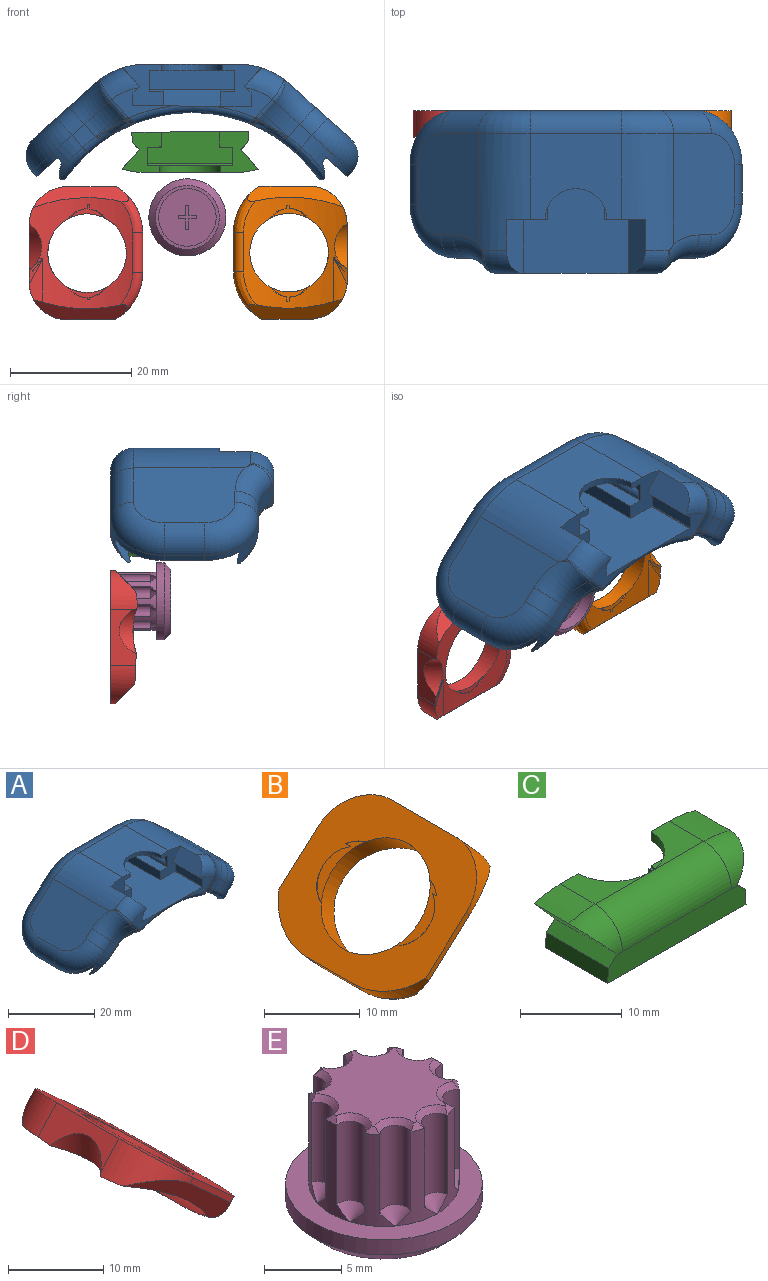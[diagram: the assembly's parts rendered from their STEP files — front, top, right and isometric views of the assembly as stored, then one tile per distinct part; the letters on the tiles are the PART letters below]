
ASSEMBLY  parts=5 mates=4
PART A: 164 faces, bbox 57.7x34x23.8 mm
  f0: cylinder r=10.41mm len=20.83mm, axis (0.67,0,-0.74), area 140.7mm2, adj f70,f71,f73,f74,f116,f122,f149,f150
  f1: plane 15.75x3.43mm, normal (1,0,0), area 24.3mm2, adj f5,f111,f112,f123,f124,f148,f150,f162
  f2: plane 15.75x3.43mm, normal (-1,0,0), area 24.3mm2, adj f3,f111,f115,f123,f124,f153,f155,f163
  f3: plane 6.94x6.69mm, normal (0,-1,0), area 27mm2, adj f2,f4,f6,f106,f107,f108,f109,f110
  f4: plane 15.11x14.14mm, normal (0,0,1), area 173.1mm2, adj f3,f5,f6,f7,f91,f125
  f5: plane 6.88x6.69mm, normal (0,-1,0), area 26.8mm2, adj f1,f4,f7,f103,f104,f105,f106,f111
  f6: cylinder r=12.7mm len=19.22mm, axis (0,1,0), area 158.4mm2, adj f3,f4,f43,f93,f100,f110,f137
  f7: cylinder r=12.7mm len=19.22mm, axis (0,1,0), area 158.4mm2, adj f4,f5,f11,f42,f89,f103,f126
  f8: plane 9.84x4.88mm, normal (0,-1,0), area 14.3mm2, adj f10,f11,f104,f105,f106,f129,f130,f131
  f9: plane 9.64x4.88mm, normal (0,-1,0), area 14mm2, adj f10,f100,f106,f107,f108,f109,f140,f141
  f10: torus R=26.58mm, axis (0,-1,0), area 38.5mm2, adj f8,f9,f12,f106,f134,f135,f136,f145
  f11: torus R=8.89mm, axis (0,-1,0), area 27.7mm2, adj f7,f8,f103,f104,f127,f128
  f12: cylinder r=25.31mm len=40.92mm, axis (0,1,0), area 321.2mm2, adj f10,f14,f20,f25,f37,f39,f60,f61
  f13: cylinder r=13.97mm len=5.07mm, axis (0,1,0), area 14.8mm2, adj f16,f26,f31,f46,f53,f74
  f14: torus R=39.28mm, axis (0,1,0), area 76.6mm2, adj f12,f16,f17,f44,f64,f65
  f15: cylinder r=13.97mm len=5.07mm, axis (0,1,0), area 14.8mm2, adj f17,f21,f30,f48,f58,f76
  f16: bspline ~6.48x5.29mm, area 7.5mm2, adj f13,f14,f46,f65,f74
  f17: bspline ~8.33x6.71mm, area 7.5mm2, adj f14,f15,f48,f64,f76
  f18: plane 22.35x6.9mm, normal (-0.67,0,-0.74), area 34.8mm2, adj f19,f22,f28,f33,f35,f117
  f19: plane 6.96x6.56mm, normal (0,1,0), area 8.6mm2, adj f18,f20,f35,f75,f117
  f20: plane 15.09x12.05mm, normal (0.47,0.71,0.53), area 38.8mm2, adj f12,f19,f35,f39,f75
  f21: plane 14.06x11.28mm, normal (0.47,-0.71,0.53), area 37.8mm2, adj f15,f22,f30,f33,f38,f76
  f22: plane 6.71x6.34mm, normal (0,-1,0), area 8.3mm2, adj f18,f21,f33,f76,f117
  f23: plane 22.35x6.9mm, normal (0.67,0,-0.74), area 34.8mm2, adj f24,f27,f29,f32,f34,f116
  f24: plane 6.96x6.56mm, normal (0,1,0), area 8.6mm2, adj f23,f25,f34,f73,f116
  f25: plane 15.09x12.05mm, normal (-0.47,0.71,0.53), area 38.8mm2, adj f12,f24,f34,f37,f73
  f26: plane 14.06x11.28mm, normal (-0.47,-0.71,0.53), area 37.8mm2, adj f13,f27,f31,f32,f36,f74
  f27: plane 6.71x6.34mm, normal (0,-1,0), area 8.3mm2, adj f23,f26,f32,f74,f116
  f28: plane 6.52x0.85mm, normal (0.74,0,-0.67), area 7.5mm2, adj f18,f33,f35,f98
  f29: plane 6.52x0.85mm, normal (-0.74,0,-0.67), area 7.5mm2, adj f23,f32,f34,f90
  f30: cylinder r=25.31mm len=9.51mm, axis (0,1,0), area 22.3mm2, adj f15,f21,f38,f59
  f31: cylinder r=25.31mm len=9.51mm, axis (0,1,0), area 22.3mm2, adj f13,f26,f36,f55
  f32: cylinder r=8.89mm len=8.89mm, axis (0.67,0,-0.74), area 23.3mm2, adj f23,f26,f27,f29,f36,f50,f88
  f33: cylinder r=8.89mm len=8.89mm, axis (0.67,0,0.74), area 23.3mm2, adj f18,f21,f22,f28,f38,f50,f97
  f34: cylinder r=8.89mm len=8.89mm, axis (0.67,0,-0.74), area 24.1mm2, adj f23,f24,f25,f29,f37,f41,f92
  f35: cylinder r=8.89mm len=8.89mm, axis (0.67,0,0.74), area 24.1mm2, adj f18,f19,f20,f28,f39,f40,f99
  f36: bspline ~7.85x7.18mm, area 13.1mm2, adj f26,f31,f32,f55
  f37: bspline ~8.21x7.4mm, area 13.8mm2, adj f12,f25,f34,f60
  f38: bspline ~7.41x6.89mm, area 13.1mm2, adj f21,f30,f33,f59
  f39: bspline ~7.85x7.18mm, area 13.8mm2, adj f12,f20,f35,f63
  f40: plane 3.86x3.78mm, normal (0,-1,0), area 7.3mm2, adj f35,f63,f77,f101
  f41: plane 3.86x3.78mm, normal (0,-1,0), area 7.3mm2, adj f34,f60,f82,f94
  f42: plane 18.19x10.02mm, normal (-0.67,0,0.74), area 216.5mm2, adj f7,f87,f88,f90,f92,f94,f96
  f43: plane 18.19x10.02mm, normal (0.67,0,0.74), area 216.5mm2, adj f6,f95,f97,f98,f99,f101,f102
  f44: cone r=29.12mm half-angle=20.6deg, axis (0,1,0), area 46.9mm2, adj f14,f45,f46,f48
  f45: torus R=15.15mm, axis (0,-1,0), area 0.3mm2, adj f44,f47,f49,f54
  f46: bspline ~10.91x6.7mm, area 18.8mm2, adj f13,f16,f44,f47,f51
  f47: bspline ~5.27x4.34mm, area 0mm2, adj f45,f46,f52
  f48: bspline ~9.02x6.04mm, area 18.8mm2, adj f15,f17,f44,f49,f57
  f49: bspline ~4.48x4.13mm, area 0mm2, adj f45,f48,f56
  f50: plane 39.49x9.87mm, normal (0,1,0), area 99.5mm2, adj f32,f33,f51,f52,f53,f54,f55,f56
  f51: bspline ~6.72x4.14mm, area 8.6mm2, adj f46,f50,f52,f53
  f52: bspline ~1.28x0.87mm, area 0.3mm2, adj f47,f50,f51,f54
  f53: torus R=12.7mm, axis (0,-1,0), area 10.1mm2, adj f13,f50,f51,f55
  f54: torus R=29.45mm, axis (0,-1,0), area 7.9mm2, adj f45,f50,f52,f56
  f55: torus R=26.58mm, axis (0,-1,0), area 15.5mm2, adj f31,f36,f50,f53
  f56: bspline ~1.25x0.84mm, area 0.3mm2, adj f49,f50,f54,f57
  f57: bspline ~6.78x4.19mm, area 8.6mm2, adj f48,f50,f56,f58
  f58: torus R=12.7mm, axis (0,-1,0), area 10.1mm2, adj f15,f50,f57,f59
  f59: torus R=26.58mm, axis (0,-1,0), area 15.5mm2, adj f30,f38,f50,f58
  f60: torus R=26.58mm, axis (0,1,0), area 8.8mm2, adj f12,f37,f41,f83,f84,f85,f86
  f61: cylinder r=1.27mm len=2.6mm, axis (0,1,0), area 0.4mm2, adj f12,f85,f135
  f62: cylinder r=1.27mm len=2.6mm, axis (0,1,0), area 0.4mm2, adj f12,f80,f147
  f63: torus R=26.58mm, axis (0,1,0), area 8.8mm2, adj f12,f39,f40,f78,f79,f80,f81
  f64: plane 9.88x2.32mm, normal (0.74,0,-0.67), area 26.5mm2, adj f12,f14,f17,f75,f76,f119
  f65: plane 9.88x2.46mm, normal (-0.74,0,-0.67), area 28.4mm2, adj f12,f14,f16,f71,f73,f74
  f66: plane 19.9x14.81mm, normal (-0.67,0,-0.74), area 308.2mm2, adj f121,f160,f161
  f67: plane 9.97x0.94mm, normal (0.67,0,0.74), area 8.5mm2, adj f68,f72
  f68: cylinder r=10.41mm len=20.83mm, axis (-0.67,0,-0.74), area 140.9mm2, adj f67,f72,f75,f76,f117,f118,f120,f121
  f69: plane 19.9x14.81mm, normal (0.67,0,-0.74), area 308.2mm2, adj f122,f158,f159
  f70: plane 9.97x0.94mm, normal (-0.67,0,0.74), area 8.5mm2, adj f0,f71
  f71: plane 16.96x4.4mm, normal (-1,0,0.05), area 33.5mm2, adj f0,f65,f70,f73,f74
  f72: plane 15.86x3.38mm, normal (1,0,0.05), area 30.3mm2, adj f67,f68,f118,f119,f120
  f73: cylinder r=6.35mm len=8.43mm, axis (0.67,0,-0.74), area 24.1mm2, adj f0,f12,f24,f25,f65,f71,f116
  f74: cylinder r=6.35mm len=8.17mm, axis (-0.67,0,0.74), area 23.2mm2, adj f0,f13,f16,f26,f27,f65,f71,f116
  f75: cylinder r=6.35mm len=8.43mm, axis (-0.67,0,-0.74), area 23.3mm2, adj f12,f19,f20,f64,f68,f117,f118
  f76: cylinder r=6.35mm len=8.17mm, axis (0.67,0,0.74), area 22.3mm2, adj f15,f17,f21,f22,f64,f68,f117,f120
  f77: cylinder r=7.62mm len=5.86mm, axis (-0.67,0,-0.74), area 16.5mm2, adj f40,f78,f102,f139,f140
  f78: bspline ~5.88x4.79mm, area 3.6mm2, adj f63,f77,f79,f141
  f79: bspline ~5.37x3.39mm, area 1.5mm2, adj f63,f78,f81,f142
  f80: bspline ~4.93x4.83mm, area 4.7mm2, adj f62,f63,f81,f146
  f81: bspline ~6.23x3.41mm, area 7.9mm2, adj f63,f79,f80,f143,f144,f145
  f82: cylinder r=7.62mm len=5.86mm, axis (0.67,0,-0.74), area 16.5mm2, adj f41,f83,f96,f128,f129
  f83: bspline ~5.39x4.52mm, area 3.6mm2, adj f60,f82,f84,f130
  f84: bspline ~5.35x3.43mm, area 1.5mm2, adj f60,f83,f86,f131
  f85: bspline ~4.93x4.83mm, area 4.7mm2, adj f60,f61,f86,f136
  f86: bspline ~6.25x3.43mm, area 7.9mm2, adj f60,f84,f85,f132,f133,f134
  f87: cylinder r=3.81mm len=8.79mm, axis (-0.74,0,-0.67), area 50.3mm2, adj f42,f50,f88,f89
  f88: torus R=5.08mm, axis (0.67,0,-0.74), area 70.6mm2, adj f32,f42,f87,f90
  f89: torus R=8.89mm, axis (0,-1,0), area 49.6mm2, adj f7,f50,f87,f91
  f90: cylinder r=3.81mm len=6.52mm, axis (0,1,0), area 39mm2, adj f29,f42,f88,f92
  f91: cylinder r=3.81mm len=15.11mm, axis (1,0,0), area 90.4mm2, adj f4,f50,f89,f93
  f92: torus R=5.08mm, axis (0.67,0,-0.74), area 70.6mm2, adj f34,f42,f90,f94
  f93: torus R=8.89mm, axis (0,-1,0), area 49.6mm2, adj f6,f50,f91,f95
  f94: cylinder r=3.81mm len=4.65mm, axis (-0.74,0,-0.67), area 16.3mm2, adj f41,f42,f92,f96
  f95: cylinder r=3.81mm len=8.79mm, axis (-0.74,0,0.67), area 50.3mm2, adj f43,f50,f93,f97
  f96: torus R=11.43mm, axis (0.67,0,-0.74), area 37.2mm2, adj f42,f82,f94,f126,f127
  f97: torus R=5.08mm, axis (-0.67,0,-0.74), area 70.6mm2, adj f33,f43,f95,f98
  f98: cylinder r=3.81mm len=6.52mm, axis (0,-1,0), area 39mm2, adj f28,f43,f97,f99
  f99: torus R=5.08mm, axis (-0.67,0,-0.74), area 70.6mm2, adj f35,f43,f98,f101
  f100: torus R=8.89mm, axis (0,-1,0), area 27.7mm2, adj f6,f9,f109,f110,f138,f139
  f101: cylinder r=3.81mm len=4.65mm, axis (-0.74,0,0.67), area 16.3mm2, adj f40,f43,f99,f102
  f102: torus R=11.43mm, axis (-0.67,0,-0.74), area 37.2mm2, adj f43,f77,f101,f137,f138
  f103: plane 8.89x3.14mm, normal (0.74,0,0.67), area 34.1mm2, adj f5,f7,f11,f104
  f104: plane 8.89x1.11mm, normal (0.67,0,-0.74), area 13.3mm2, adj f5,f8,f11,f103,f105
  f105: plane 8.89x2.11mm, normal (1,0,-0.05), area 18.8mm2, adj f5,f8,f104,f106
  f106: plane 20.03x19.46mm, normal (0,0,1), area 278.7mm2, adj f3,f5,f8,f9,f10,f105,f107,f113
  f107: plane 8.89x0.23mm, normal (0,0,1), area 2mm2, adj f3,f9,f106,f108
  f108: plane 8.89x2.19mm, normal (-1,0,-0.05), area 19.5mm2, adj f3,f9,f107,f109
  f109: plane 8.89x1.11mm, normal (-0.67,0,-0.74), area 13.3mm2, adj f3,f9,f100,f108,f110
  f110: plane 8.89x3.14mm, normal (-0.74,0,0.67), area 34.1mm2, adj f3,f6,f100,f109
  f111: plane 15.75x14.1mm, normal (0,0,-1), area 181.5mm2, adj f1,f2,f3,f5,f123,f125
  f112: plane 15.11x2.29mm, normal (0,0,1), area 34.6mm2, adj f1,f5,f113,f124
  f113: plane 15.11x2.39mm, normal (1,0,0), area 31.3mm2, adj f5,f106,f112,f124
  f114: plane 15.11x2.42mm, normal (-1,0,0), area 31.7mm2, adj f3,f106,f115,f124
  f115: plane 15.11x2.29mm, normal (0,0,1), area 34.6mm2, adj f2,f3,f114,f124
  f116: cone r=11.43mm half-angle=53.1deg, axis (0.67,0,-0.74), area 51.3mm2, adj f0,f23,f24,f27,f73,f74
  f117: cone r=11.43mm half-angle=53.1deg, axis (-0.67,0,-0.74), area 51.3mm2, adj f18,f19,f22,f68,f75,f76
  f118: bspline ~3.66x1.79mm, area 1.4mm2, adj f68,f72,f75,f119
  f119: cylinder r=0.46mm len=9.65mm, axis (0,1,0), area 3.5mm2, adj f64,f72,f118,f120
  f120: bspline ~3.66x1.79mm, area 1.4mm2, adj f68,f72,f76,f119
  f121: cone r=10.41mm half-angle=45deg, axis (-0.67,0,-0.74), area 45.9mm2, adj f66,f68,f153
  f122: cone r=10.41mm half-angle=45deg, axis (0.67,0,-0.74), area 45.9mm2, adj f0,f69,f148
  f123: plane 14.1x3.05mm, normal (0,-1,0), area 43mm2, adj f1,f2,f111,f124
  f124: plane 14.1x4.67mm, normal (0,-0.51,0.86), area 55mm2, adj f1,f2,f106,f112,f113,f114,f115,f123
  f125: cylinder r=5.08mm len=10.16mm, axis (0,0,1), area 17mm2, adj f3,f4,f5,f111
  f126: bspline ~1.74x1.04mm, area 0.1mm2, adj f7,f96,f127
  f127: bspline ~4.04x3.97mm, area 3.3mm2, adj f11,f96,f126,f128
  f128: bspline ~1.32x1.28mm, area 0mm2, adj f11,f82,f127,f129
  f129: cylinder r=1.02mm len=2.52mm, axis (0.67,0,-0.74), area 2.2mm2, adj f8,f82,f128,f130
  f130: bspline ~1.65x1.59mm, area 0.9mm2, adj f8,f83,f129,f131
  f131: bspline ~0.94x0.85mm, area 0.2mm2, adj f8,f84,f130,f132
  f132: bspline ~0.87x0.53mm, area 0.1mm2, adj f86,f131,f133
  f133: bspline ~0.99x0.71mm, area 0.3mm2, adj f8,f86,f132,f134
  f134: bspline ~1.25x1.17mm, area 0.9mm2, adj f10,f86,f133,f136
  f135: bspline ~0.61x0.6mm, area 0mm2, adj f10,f61,f136
  f136: bspline ~0.85x0.51mm, area 0.2mm2, adj f10,f85,f134,f135
  f137: bspline ~3.54x1.99mm, area 0.1mm2, adj f6,f102,f138
  f138: bspline ~4.04x3.97mm, area 3.3mm2, adj f100,f102,f137,f139
  f139: bspline ~1.32x1.28mm, area 0mm2, adj f77,f100,f138,f140
  f140: cylinder r=1.02mm len=2.52mm, axis (-0.67,0,-0.74), area 2.2mm2, adj f9,f77,f139,f141
  f141: bspline ~2.3x2.18mm, area 0.9mm2, adj f9,f78,f140,f142
  f142: bspline ~0.94x0.85mm, area 0.2mm2, adj f9,f79,f141,f143
  f143: bspline ~0.87x0.53mm, area 0.1mm2, adj f81,f142,f144
  f144: bspline ~1x0.74mm, area 0.2mm2, adj f9,f81,f143,f145
  f145: bspline ~1.25x1.19mm, area 0.9mm2, adj f10,f81,f144,f146
  f146: bspline ~0.91x0.55mm, area 0.2mm2, adj f10,f80,f145,f147
  f147: bspline ~0.61x0.6mm, area 0mm2, adj f10,f62,f146
  f148: extruded ~13.72x4.79mm, area 54.2mm2, adj f1,f122,f149,f150,f151,f152,f162
  f149: plane 11.88x3.52mm, normal (0,0,1), area 25.3mm2, adj f0,f148,f150,f152,f162
  f150: plane 4.79x1.79mm, normal (0,1,0), area 2.8mm2, adj f0,f1,f148,f149,f151,f162
  f151: plane 0.77x0.64mm, normal (1,0,0), area 0.1mm2, adj f0,f148,f150
  f152: plane 1.9x0.83mm, normal (1,0,0), area 0.4mm2, adj f0,f148,f149
  f153: extruded ~13.72x4.79mm, area 54.2mm2, adj f2,f121,f154,f155,f156,f157,f163
  f154: plane 11.89x3.53mm, normal (0,0,1), area 25.3mm2, adj f68,f153,f155,f157,f163
  f155: plane 4.79x1.79mm, normal (0,1,0), area 2.8mm2, adj f2,f68,f153,f154,f156,f163
  f156: plane 0.77x0.64mm, normal (-1,0,0), area 0.1mm2, adj f68,f153,f155
  f157: plane 1.9x0.83mm, normal (-1,0,0), area 0.4mm2, adj f68,f153,f154
  f158: plane 2.25x0.04mm, normal (1,0,0), area 0.1mm2, adj f69,f159
  f159: extruded ~2.25x0.04mm, area 0mm2, adj f69,f158
  f160: plane 2.25x0.04mm, normal (-1,0,0), area 0.1mm2, adj f66,f161
  f161: extruded ~2.25x0.04mm, area 0mm2, adj f66,f160
  f162: cylinder r=1.27mm len=13.72mm, axis (0,-1,0), area 25.5mm2, adj f1,f148,f149,f150
  f163: cylinder r=1.27mm len=13.72mm, axis (0,1,0), area 25.5mm2, adj f2,f153,f154,f155
PART B: 36 faces, bbox 20x23.9x18.1 mm
  f0: cylinder r=25.31mm len=18.28mm, axis (0,1,0), area 126.4mm2, adj f2,f3,f4,f5,f6,f7,f8,f9
  f1: plane 21.95x13.89mm, normal (-0.67,0,0.74), area 225.5mm2, adj f10,f11,f13,f14,f17,f18,f19,f22
  f2: cylinder r=3.24mm len=1.7mm, axis (0.67,0,-0.74), area 0mm2, adj f0,f9,f34
  f3: cylinder r=3.24mm len=2.01mm, axis (0.67,0,-0.74), area 0.1mm2, adj f0,f8,f29,f34
  f4: cylinder r=3.24mm len=2.01mm, axis (0.67,0,-0.74), area 0.1mm2, adj f0,f6,f29,f32
  f5: cylinder r=3.24mm len=1.7mm, axis (0.67,0,-0.74), area 0mm2, adj f0,f7,f32
  f6: bspline ~4.55x2.83mm, area 0.3mm2, adj f0,f4,f29
  f7: bspline ~4.55x2.65mm, area 0.3mm2, adj f0,f5,f29
  f8: bspline ~4.55x2.83mm, area 0.3mm2, adj f0,f3,f29
  f9: bspline ~4.55x2.65mm, area 0.3mm2, adj f0,f2,f29
  f10: cone r=3.75mm half-angle=45deg, axis (-0.67,0,0.74), area 0.3mm2, adj f1,f29,f35
  f11: cone r=3.75mm half-angle=45deg, axis (-0.67,0,0.74), area 0.3mm2, adj f1,f29,f31
  f12: torus R=39.28mm, axis (0,1,0), area 0.4mm2, adj f0,f13,f25,f28
  f13: plane 9.51x3.46mm, normal (0.74,0,0.67), area 24.4mm2, adj f1,f12,f14,f25,f27,f28
  f14: cylinder r=6.35mm len=7.69mm, axis (-0.67,0,0.74), area 26.3mm2, adj f0,f1,f13,f23,f24,f28
  f15: cylinder r=1.27mm len=6.52mm, axis (0,1,0), area 15.5mm2, adj f0,f16,f18,f20
  f16: bspline ~9.5x4.45mm, area 15.4mm2, adj f0,f15,f17,f24
  f17: cylinder r=8.89mm len=7.63mm, axis (0.67,0,-0.74), area 18.3mm2, adj f1,f16,f18,f23,f24
  f18: plane 6.52x1.85mm, normal (-0.74,0,-0.67), area 16.2mm2, adj f1,f15,f17,f19
  f19: cylinder r=8.89mm len=7.8mm, axis (0.67,0,-0.74), area 18.8mm2, adj f1,f18,f20,f21,f22
  f20: bspline ~9.84x4.9mm, area 16.1mm2, adj f0,f15,f19,f21
  f21: plane 14.42x11.77mm, normal (0.47,0.71,-0.53), area 39.2mm2, adj f0,f19,f20,f22,f26,f27
  f22: plane 6.23x5.71mm, normal (0,1,0), area 5.6mm2, adj f1,f19,f21,f27
  f23: plane 6.45x5.91mm, normal (0,-1,0), area 5.8mm2, adj f1,f14,f17,f24
  f24: plane 14.65x11.84mm, normal (0.47,-0.71,-0.53), area 40mm2, adj f0,f14,f16,f17,f23
  f25: bspline ~4.3x3.46mm, area 3mm2, adj f12,f13,f26,f27
  f26: cylinder r=13.97mm len=7.21mm, axis (0,1,0), area 10.1mm2, adj f0,f21,f25,f27
  f27: cylinder r=6.35mm len=7.48mm, axis (0.67,0,-0.74), area 25.7mm2, adj f1,f13,f21,f22,f25,f26
  f28: cylinder r=4.57mm len=7.54mm, axis (0,0,-1), area 17.8mm2, adj f0,f12,f13,f14
  f29: cylinder r=6.48mm len=12.95mm, axis (0.68,0,-0.74), area 120.6mm2, adj f0,f1,f3,f4,f6,f7,f8,f9
  f30: cylinder r=4.51mm len=2.07mm, axis (0.68,0,-0.74), area 0mm2, adj f1,f29,f31
  f31: plane 5.8x5.31mm, normal (-0.68,0,0.74), area 7.7mm2, adj f1,f11,f29,f30
  f32: plane 3.94x3.61mm, normal (0.68,0,-0.74), area 3.5mm2, adj f0,f4,f5,f29
  f33: cylinder r=4.41mm len=1.85mm, axis (0.68,0,-0.74), area 0mm2, adj f1,f29,f35
  f34: plane 3.94x3.61mm, normal (0.68,0,-0.74), area 3.4mm2, adj f0,f2,f3,f29
  f35: plane 5.75x5.26mm, normal (-0.68,0,0.74), area 7.5mm2, adj f1,f10,f29,f33
PART C: 31 faces, bbox 22.5x8.6x6.9 mm
  f0: plane 6.71x6.45mm, normal (0,1,0), area 24.9mm2, adj f2,f3,f9,f10,f14,f16,f17,f18
  f1: plane 7.55x4.83mm, normal (0,0,1), area 17.5mm2, adj f4,f5,f13,f26
  f2: plane 7.55x4.83mm, normal (0,0,1), area 17.5mm2, adj f0,f5,f14,f26
  f3: plane 19.21x8.64mm, normal (0,0,-1), area 105.4mm2, adj f0,f4,f7,f15,f16,f19,f20,f24
  f4: plane 6.65x6.45mm, normal (0,1,0), area 24.7mm2, adj f1,f3,f11,f12,f13,f15,f20,f21
  f5: cylinder r=3.81mm len=15.11mm, axis (1,0,0), area 90.4mm2, adj f1,f2,f6,f7,f8
  f6: torus R=8.89mm, axis (0,-1,0), area 15.8mm2, adj f5,f7,f9,f10,f14
  f7: plane 19.21x2.9mm, normal (0,-1,0), area 53.4mm2, adj f3,f5,f6,f8,f9,f12,f15,f16
  f8: torus R=8.89mm, axis (0,-1,0), area 15.8mm2, adj f5,f7,f11,f12,f13
  f9: plane 8.64x1.21mm, normal (0.67,0,0.74), area 14.1mm2, adj f0,f6,f7,f10,f16
  f10: plane 8.64x3.23mm, normal (0.74,0,-0.67), area 34mm2, adj f0,f6,f9,f14
  f11: plane 8.64x3.23mm, normal (-0.74,0,-0.67), area 34mm2, adj f4,f8,f12,f13
  f12: plane 8.64x1.21mm, normal (-0.67,0,0.74), area 14.1mm2, adj f4,f7,f8,f11,f15
  f13: cylinder r=12.7mm len=4.83mm, axis (0,1,0), area 17.9mm2, adj f1,f4,f8,f11
  f14: cylinder r=12.7mm len=4.83mm, axis (0,1,0), area 17.9mm2, adj f0,f2,f6,f10
  f15: plane 8.64x1.78mm, normal (-1,0,0.05), area 15.4mm2, adj f3,f4,f7,f12
  f16: plane 8.64x1.85mm, normal (1,0,0.05), area 16mm2, adj f0,f3,f7,f9
  f17: plane 6.35x3.05mm, normal (-1,0,0), area 19.3mm2, adj f0,f18,f23,f24,f25
  f18: plane 6.35x2.29mm, normal (0,0,1), area 14.2mm2, adj f0,f17,f19,f24,f30
  f19: plane 6.35x2.57mm, normal (-1,0,0), area 16mm2, adj f0,f3,f18,f24,f29,f30
  f20: plane 6.35x2.54mm, normal (1,0,0), area 15.8mm2, adj f3,f4,f21,f24,f27,f28
  f21: plane 6.35x2.29mm, normal (0,0,1), area 14.2mm2, adj f4,f20,f22,f24,f27
  f22: plane 6.35x3.05mm, normal (1,0,0), area 19.3mm2, adj f4,f21,f23,f24,f25
  f23: plane 14.1x5.97mm, normal (0,0,-1), area 46.2mm2, adj f0,f4,f17,f22,f25,f26
  f24: plane 14.1x5.24mm, normal (0,1,0), area 62mm2, adj f3,f17,f18,f19,f20,f21,f22,f25
  f25: plane 14.1x0.38mm, normal (0,0.71,-0.71), area 7.6mm2, adj f17,f22,f23,f24
  f26: cylinder r=5.08mm len=10.15mm, axis (0,0,1), area 16.5mm2, adj f0,f1,f2,f4,f23
  f27: cylinder r=5.08mm len=1.51mm, axis (0,0,1), area 0.4mm2, adj f4,f20,f21,f28
  f28: plane 1.51x0.31mm, normal (0,0,1), area 0.3mm2, adj f4,f20,f27
  f29: plane 1.51x0.31mm, normal (0,0,1), area 0.3mm2, adj f0,f19,f30
  f30: cylinder r=5.08mm len=1.51mm, axis (0,0,1), area 0.4mm2, adj f0,f18,f19,f29
PART D: 37 faces, bbox 20x23.9x18.1 mm
  f0: cylinder r=3.24mm len=1.7mm, axis (-0.67,0,-0.74), area 0mm2, adj f5,f7,f36
  f1: cone r=3.75mm half-angle=45deg, axis (0.67,0,0.74), area 0.3mm2, adj f22,f29,f35
  f2: cylinder r=3.24mm len=2.01mm, axis (-0.67,0,-0.74), area 0.1mm2, adj f5,f10,f29,f33
  f3: cone r=3.75mm half-angle=45deg, axis (0.67,0,0.74), area 0.8mm2, adj f22,f29,f30,f32
  f4: torus R=39.28mm, axis (0,1,0), area 0.4mm2, adj f5,f19,f26,f28
  f5: cylinder r=25.31mm len=18.28mm, axis (0,1,0), area 126.6mm2, adj f0,f2,f4,f6,f7,f8,f9,f10
  f6: cylinder r=6.35mm len=7.69mm, axis (-0.67,0,-0.74), area 26.3mm2, adj f5,f22,f23,f24,f26,f28
  f7: bspline ~4.55x2.65mm, area 0.3mm2, adj f0,f5,f29
  f8: bspline ~4.55x2.83mm, area 0.3mm2, adj f5,f15,f29
  f9: bspline ~4.55x2.65mm, area 0.3mm2, adj f5,f16,f29
  f10: bspline ~4.55x2.83mm, area 0.3mm2, adj f2,f5,f29
  f11: cylinder r=1.27mm len=6.52mm, axis (0,1,0), area 15.5mm2, adj f5,f12,f13,f17
  f12: bspline ~9.03x3.93mm, area 15.4mm2, adj f5,f11,f14,f24
  f13: plane 6.52x1.85mm, normal (0.74,0,-0.67), area 16.2mm2, adj f11,f14,f18,f22
  f14: cylinder r=8.89mm len=7.63mm, axis (0.67,0,0.74), area 18.3mm2, adj f12,f13,f22,f23,f24
  f15: cylinder r=3.24mm len=2.01mm, axis (-0.67,0,-0.74), area 0.1mm2, adj f5,f8,f29,f36
  f16: cylinder r=3.24mm len=1.7mm, axis (-0.67,0,-0.74), area 0mm2, adj f5,f9,f33
  f17: bspline ~9.5x4.45mm, area 16.1mm2, adj f5,f11,f18,f20
  f18: cylinder r=8.89mm len=7.8mm, axis (0.67,0,0.74), area 18.8mm2, adj f13,f17,f20,f21,f22
  f19: bspline ~4.3x3.46mm, area 3mm2, adj f4,f25,f26,f27
  f20: plane 14.42x11.78mm, normal (-0.47,0.71,-0.53), area 39.1mm2, adj f5,f17,f18,f21,f25,f27
  f21: plane 6.23x5.71mm, normal (0,1,0), area 5.6mm2, adj f18,f20,f22,f27
  f22: plane 21.95x13.9mm, normal (0.67,0,0.74), area 225.9mm2, adj f1,f3,f6,f13,f14,f18,f21,f23
  f23: plane 6.45x5.91mm, normal (0,-1,0), area 5.8mm2, adj f6,f14,f22,f24
  f24: plane 14.65x11.84mm, normal (-0.47,-0.71,-0.53), area 40mm2, adj f5,f6,f12,f14,f23
  f25: cylinder r=13.97mm len=7.21mm, axis (0,1,0), area 10.1mm2, adj f5,f19,f20,f27
  f26: plane 9.51x3.46mm, normal (-0.74,0,0.67), area 24.4mm2, adj f4,f6,f19,f22,f27,f28
  f27: cylinder r=6.35mm len=7.48mm, axis (0.67,0,0.74), area 25.7mm2, adj f19,f20,f21,f22,f25,f26
  f28: cylinder r=4.57mm len=7.54mm, axis (0,0,-1), area 17.8mm2, adj f4,f5,f6,f26
  f29: cylinder r=6.48mm len=12.95mm, axis (-0.68,0,-0.74), area 120.4mm2, adj f1,f2,f3,f5,f7,f8,f9,f10
  f30: plane 5.37x4.91mm, normal (0.68,0,0.74), area 6.7mm2, adj f3,f22,f29,f31,f32
  f31: cylinder r=4.07mm len=1.12mm, axis (-0.68,0,-0.74), area 0mm2, adj f22,f29,f30
  f32: cylinder r=4.07mm len=3.48mm, axis (-0.68,0,-0.74), area 0mm2, adj f3,f30
  f33: plane 3.94x3.61mm, normal (-0.68,0,-0.74), area 3.3mm2, adj f2,f5,f16,f29
  f34: cylinder r=4.48mm len=2.21mm, axis (-0.68,0,-0.74), area 0mm2, adj f22,f29,f35
  f35: plane 5.85x5.36mm, normal (0.68,0,0.74), area 7.8mm2, adj f1,f22,f29,f34
  f36: plane 3.94x3.61mm, normal (-0.68,0,-0.74), area 3.5mm2, adj f0,f5,f15,f29
PART E: 70 faces, bbox 12.7x12.7x9.9 mm
  f0: plane 9.47x9.47mm, normal (0,0,-1), area 67.3mm2, adj f24,f36,f37,f38,f39,f40,f41,f42
  f1: cylinder r=1.02mm len=6.27mm, axis (0,0,-1), area 18.7mm2, adj f2,f20,f33,f68
  f2: cylinder r=4.85mm len=7.24mm, axis (0,0,-1), area 8.3mm2, adj f1,f3,f22,f32,f33,f66
  f3: cylinder r=1.02mm len=6.27mm, axis (0,0,-1), area 18.7mm2, adj f2,f4,f32,f64
  f4: cylinder r=4.85mm len=7.24mm, axis (0,0,-1), area 8.3mm2, adj f3,f5,f22,f31,f32,f62
  f5: cylinder r=1.02mm len=6.27mm, axis (0,0,-1), area 18.7mm2, adj f4,f6,f31,f60
  f6: cylinder r=4.85mm len=7.24mm, axis (0,0,-1), area 8.3mm2, adj f5,f7,f22,f30,f31,f58
  f7: cylinder r=1.02mm len=6.27mm, axis (0,0,-1), area 18.7mm2, adj f6,f8,f30,f56
  f8: cylinder r=4.85mm len=7.24mm, axis (0,0,-1), area 8.3mm2, adj f7,f9,f22,f29,f30,f54
  f9: cylinder r=1.02mm len=6.27mm, axis (0,0,-1), area 18.7mm2, adj f8,f10,f29,f52
  f10: cylinder r=4.85mm len=7.24mm, axis (0,0,-1), area 8.3mm2, adj f9,f11,f22,f28,f29,f50
  f11: cylinder r=1.02mm len=6.27mm, axis (0,0,-1), area 18.7mm2, adj f10,f12,f28,f49
  f12: cylinder r=4.85mm len=7.24mm, axis (0,0,-1), area 8.3mm2, adj f11,f13,f22,f27,f28,f51
  f13: cylinder r=1.02mm len=6.27mm, axis (0,0,-1), area 18.7mm2, adj f12,f14,f27,f53
  f14: cylinder r=4.85mm len=7.24mm, axis (0,0,-1), area 8.3mm2, adj f13,f15,f22,f26,f27,f55
  f15: cylinder r=1.02mm len=6.27mm, axis (0,0,-1), area 18.7mm2, adj f14,f16,f26,f57
  f16: cylinder r=4.85mm len=7.24mm, axis (0,0,-1), area 8.3mm2, adj f15,f17,f22,f26,f35,f59
  f17: cylinder r=1.02mm len=6.27mm, axis (0,0,-1), area 18.7mm2, adj f16,f18,f35,f61
  f18: cylinder r=4.85mm len=7.24mm, axis (0,0,-1), area 8.3mm2, adj f17,f19,f22,f34,f35,f63
  f19: cylinder r=1.02mm len=6.27mm, axis (0,0,-1), area 18.7mm2, adj f18,f20,f34,f65
  f20: cylinder r=4.85mm len=7.24mm, axis (0,0,-1), area 8.3mm2, adj f1,f19,f22,f33,f34,f67
  f21: plane 8.94x8.57mm, normal (0,0,1), area 44.3mm2, adj f49,f50,f51,f52,f53,f54,f55,f56
  f22: plane 12.7x12.7mm, normal (0,0,1), area 52.8mm2, adj f2,f4,f6,f8,f10,f12,f14,f16
  f23: cylinder r=6.35mm len=12.7mm, axis (0,0,1), area 47.6mm2, adj f22,f69
  f24: cylinder r=4.74mm len=9.47mm, axis (0,0,1), area 60.5mm2, adj f0,f25
  f25: plane 10.52x10.52mm, normal (0,0,-1), area 16.3mm2, adj f24,f69
  f26: cone r=0.05mm half-angle=45deg, axis (0,0,1), area 2.2mm2, adj f14,f15,f16,f22
  f27: cone r=0.05mm half-angle=45deg, axis (0,0,1), area 2.2mm2, adj f12,f13,f14,f22
  f28: cone r=0.05mm half-angle=45deg, axis (0,0,1), area 2.2mm2, adj f10,f11,f12,f22
  f29: cone r=0.05mm half-angle=45deg, axis (0,0,1), area 2.2mm2, adj f8,f9,f10,f22
  f30: cone r=0.05mm half-angle=45deg, axis (0,0,1), area 2.2mm2, adj f6,f7,f8,f22
  f31: cone r=0.05mm half-angle=45deg, axis (0,0,1), area 2.2mm2, adj f4,f5,f6,f22
  f32: cone r=0.05mm half-angle=45deg, axis (0,0,1), area 2.2mm2, adj f2,f3,f4,f22
  f33: cone r=0.05mm half-angle=45deg, axis (0,0,1), area 2.2mm2, adj f1,f2,f20,f22
  f34: cone r=0.05mm half-angle=45deg, axis (0,0,1), area 2.2mm2, adj f18,f19,f20,f22
  f35: cone r=0.05mm half-angle=45deg, axis (0,0,1), area 2.2mm2, adj f16,f17,f18,f22
  f36: plane 0.76x0.51mm, normal (0,-1,0), area 0.4mm2, adj f0,f37,f47,f48
  f37: plane 1.73x0.76mm, normal (-1,0,0), area 1.3mm2, adj f0,f36,f38,f48
  f38: plane 1.21x0.76mm, normal (0,-1,0), area 0.9mm2, adj f0,f37,f39,f48
  f39: plane 0.76x0.51mm, normal (-1,0,0), area 0.4mm2, adj f0,f38,f40,f48
  f40: plane 1.21x0.76mm, normal (0,1,0), area 0.9mm2, adj f0,f39,f41,f48
  f41: plane 1.73x0.76mm, normal (-1,0,0), area 1.3mm2, adj f0,f40,f42,f48
  f42: plane 0.76x0.51mm, normal (0,1,0), area 0.4mm2, adj f0,f41,f43,f48
  f43: plane 1.73x0.76mm, normal (1,0,0), area 1.3mm2, adj f0,f42,f44,f48
  f44: plane 1.21x0.76mm, normal (0,1,0), area 0.9mm2, adj f0,f43,f45,f48
  f45: plane 0.76x0.51mm, normal (1,0,0), area 0.4mm2, adj f0,f44,f46,f48
  f46: plane 1.21x0.76mm, normal (0,-1,0), area 0.9mm2, adj f0,f45,f47,f48
  f47: plane 1.73x0.76mm, normal (1,0,0), area 1.3mm2, adj f0,f36,f46,f48
  f48: plane 3.96x2.92mm, normal (0,0,-1), area 3.2mm2, adj f36,f37,f38,f39,f40,f41,f42,f43
  f49: cone r=1.02mm half-angle=45deg, axis (0,0,1), area 1.7mm2, adj f11,f21,f50,f51
  f50: cone r=4.47mm half-angle=45deg, axis (0,0,-1), area 0.3mm2, adj f10,f21,f49,f52
  f51: cone r=4.47mm half-angle=45deg, axis (0,0,-1), area 0.3mm2, adj f12,f21,f49,f53
  f52: cone r=1.02mm half-angle=45deg, axis (0,0,1), area 1.7mm2, adj f9,f21,f50,f54
  f53: cone r=1.02mm half-angle=45deg, axis (0,0,1), area 1.7mm2, adj f13,f21,f51,f55
  f54: cone r=4.47mm half-angle=45deg, axis (0,0,-1), area 0.3mm2, adj f8,f21,f52,f56
  f55: cone r=4.47mm half-angle=45deg, axis (0,0,-1), area 0.3mm2, adj f14,f21,f53,f57
  f56: cone r=1.02mm half-angle=45deg, axis (0,0,1), area 1.7mm2, adj f7,f21,f54,f58
  f57: cone r=1.02mm half-angle=45deg, axis (0,0,1), area 1.7mm2, adj f15,f21,f55,f59
  f58: cone r=4.47mm half-angle=45deg, axis (0,0,-1), area 0.3mm2, adj f6,f21,f56,f60
  f59: cone r=4.47mm half-angle=45deg, axis (0,0,-1), area 0.3mm2, adj f16,f21,f57,f61
  f60: cone r=1.02mm half-angle=45deg, axis (0,0,1), area 1.7mm2, adj f5,f21,f58,f62
  f61: cone r=1.02mm half-angle=45deg, axis (0,0,1), area 1.7mm2, adj f17,f21,f59,f63
  f62: cone r=4.47mm half-angle=45deg, axis (0,0,-1), area 0.3mm2, adj f4,f21,f60,f64
  f63: cone r=4.47mm half-angle=45deg, axis (0,0,-1), area 0.3mm2, adj f18,f21,f61,f65
  f64: cone r=1.02mm half-angle=45deg, axis (0,0,1), area 1.7mm2, adj f3,f21,f62,f66
  f65: cone r=1.02mm half-angle=45deg, axis (0,0,1), area 1.7mm2, adj f19,f21,f63,f67
  f66: cone r=4.47mm half-angle=45deg, axis (0,0,-1), area 0.3mm2, adj f2,f21,f64,f68
  f67: cone r=4.47mm half-angle=45deg, axis (0,0,-1), area 0.3mm2, adj f20,f21,f65,f68
  f68: cone r=1.02mm half-angle=45deg, axis (0,0,1), area 1.7mm2, adj f1,f21,f66,f67
  f69: cone r=5.26mm half-angle=45deg, axis (0,0,1), area 56.3mm2, adj f23,f25
PLACE A t=(19.94,-3.69,0.27)mm fixed
PLACE B rot(axis=(-0.88,0.34,-0.34),97.4deg) t=(35.93,-4.85,17.14)mm
PLACE C rot(axis=(1,0,0),180deg) t=(19.63,22.9,48.95)mm
PLACE D rot(axis=(-0.88,-0.34,0.34),97.4deg) t=(2.67,-4.85,17.05)mm
PLACE E rot(axis=(-1,0,0),90deg) t=(19.18,15.41,8.3)mm
MATE planar D.f22 <-> B.f1  axis (0,1,0) through (-0.54,23.03,13.37)mm
MATE planar B.f1 <-> E.f8  axis (0,1,0) through (36.36,23.03,2.52)mm
MATE planar B.f1 <-> A.f50  axis (0,1,0) through (40.35,23.03,-2.22)mm
MATE planar C.f7 <-> D.f22  axis (0,1,0) through (19.68,23.03,20.96)mm
